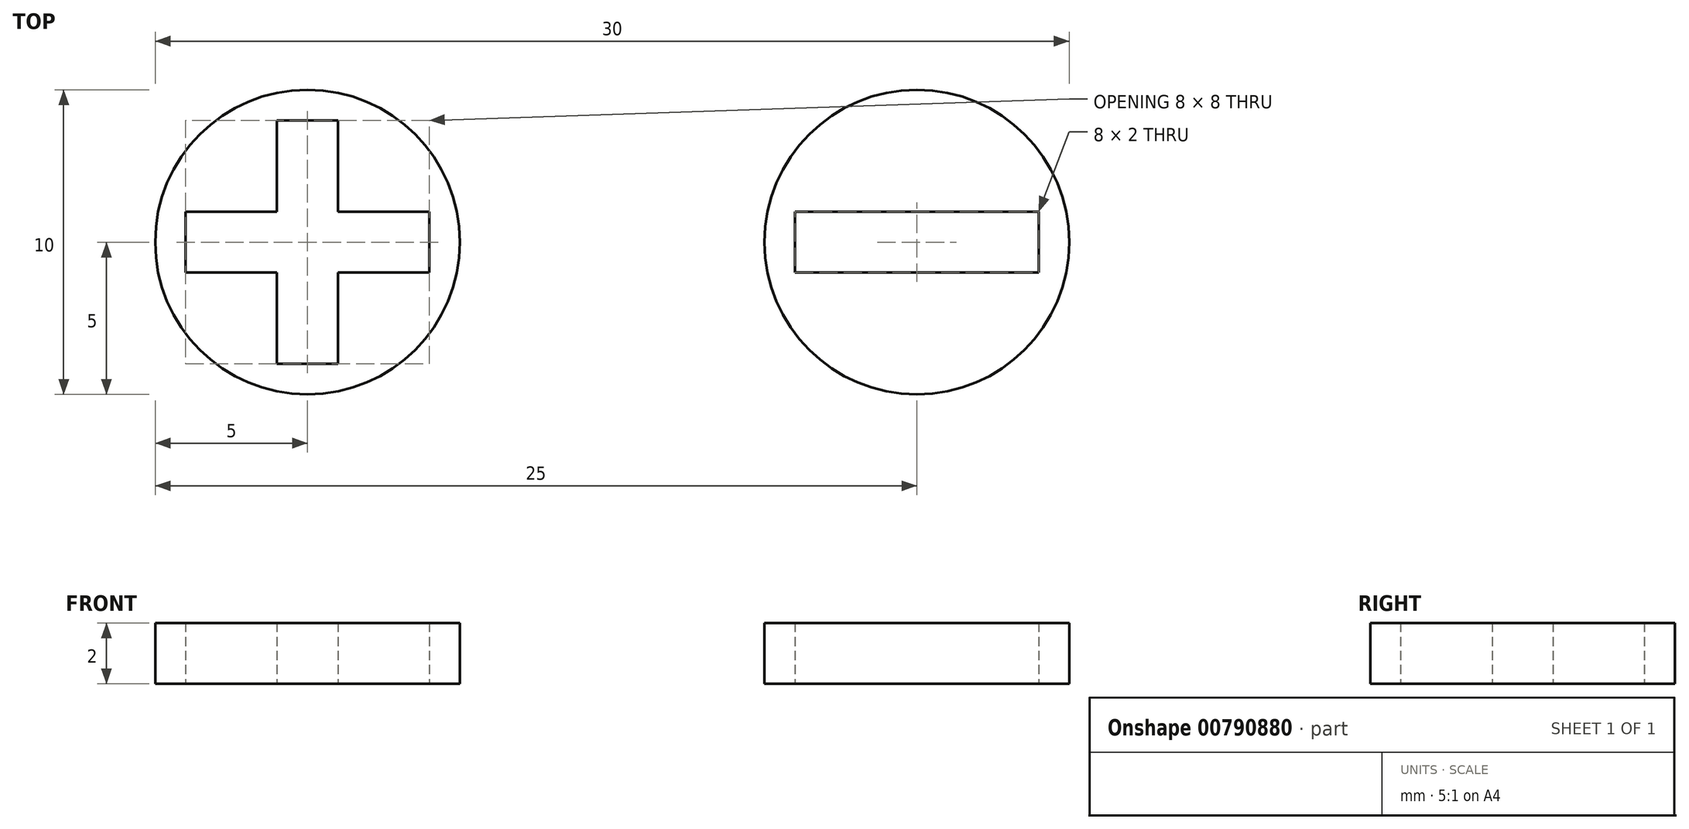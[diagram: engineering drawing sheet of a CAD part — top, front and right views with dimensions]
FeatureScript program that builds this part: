
annotation { "Feature Type Name" : "Feature", "Feature Type Description" : "" }
export const myFeature = defineFeature(function(context is Context, id is Id, definition is map)
    precondition{}
    {
        {
            var Q0;
            Q0=qCreatedBy(makeId("Top.planeOp"),FACE);
            var sketch = newSketch(context, id + "F0", { "sketchPlane" : qUnion([Q0])});
            skCircle(sketch, "E0", {"center": v(-10, 0) * mm, "radius": 5 * mm});
            skLineSegment(sketch, "E1.bottom", {"start": v(-9, 4) * mm, "end": v(-11, 4) * mm});
            skLineSegment(sketch, "E1.top", {"start": v(-9, -4) * mm, "end": v(-11, -4) * mm});
            skLineSegment(sketch, "E1.left", {"start": v(-9, 4) * mm, "end": v(-9, -4) * mm});
            skLineSegment(sketch, "E1.right", {"start": v(-11, 4) * mm, "end": v(-11, -4) * mm});
            skLineSegment(sketch, "E2.1.1", {"start": v(-6, -1) * mm, "end": v(-14, -1) * mm});
            skLineSegment(sketch, "E2.1.2", {"start": v(-6, -1) * mm, "end": v(-6, 1) * mm});
            skLineSegment(sketch, "E2.1.3", {"start": v(-6, 1) * mm, "end": v(-14, 1) * mm});
            skLineSegment(sketch, "E2.1.4", {"start": v(-14, -1) * mm, "end": v(-14, 1) * mm});
            skLineSegment(sketch, "E2.anchor1", {"start": v(-10, 0) * mm, "end": v(-9, -4) * mm, "construction": true});
            skLineSegment(sketch, "E2.anchor2", {"start": v(-10, 0) * mm, "end": v(-14, -1) * mm, "construction": true});
            skCircle(sketch, "E3.1.0.0", {"center": v(10, 0) * mm, "radius": 5 * mm});
            skLineSegment(sketch, "E3.1.0.1", {"start": v(14, 1) * mm, "end": v(6, 1) * mm});
            skLineSegment(sketch, "E3.1.0.2", {"start": v(6, -1) * mm, "end": v(6, 1) * mm});
            skLineSegment(sketch, "E3.1.0.3", {"start": v(14, -1) * mm, "end": v(6, -1) * mm});
            skLineSegment(sketch, "E3.1.0.4", {"start": v(14, -1) * mm, "end": v(14, 1) * mm});
            skLineSegment(sketch, "E3.direction1", {"start": v(-10, 0) * mm, "end": v(10, 0) * mm, "construction": true});
            skSolve(sketch);
        }
        {
            var Q0;
            Q0=makeQuery(id+"F0.imprint","IMPRINT",FACE,{"disambiguationData":[TD([[makeQuery(id+"F0.imprint","IMPRINT",EDGE,{"derivedFrom":sQuery(id+"F0.wireOp",EDGE,"E0")}),1.0]])]});
            var Q1;
            Q1=makeQuery(id+"F0.imprint","IMPRINT",FACE,{"disambiguationData":[TD([[makeQuery(id+"F0.imprint","IMPRINT",EDGE,{"derivedFrom":sQuery(id+"F0.wireOp",EDGE,"E3.1.0.0")}),1.0]])]});
            extrude(context, id + "F1", {"entities" : qUnion([Q0, Q1]), "depth" : 2 * mm, "offsetDistance" : 25 * mm});
        }
    });
